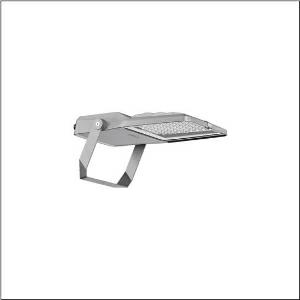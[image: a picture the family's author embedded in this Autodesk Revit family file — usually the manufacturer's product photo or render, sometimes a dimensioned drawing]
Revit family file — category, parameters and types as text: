
# Revit family: floodlight_fl_21_iq_mini___pl33t_5xa7771c4f1a_a815
name_source: partatom
category: Lighting Fixtures
units: mm (PartAtom-declared; Revit-internal decimal feet)

## family parameters
Cut with Voids When Loaded = No
Host = Face
Light Source = No
Part Type = Normal
Room Calculation Point = No
Round Connector Dimension = Use Diameter
Shared = No

## types (1)
- --- (1 x LED, 12570 lm, 87.2 W, 4000K)
    Apparent Load = 87 VA
    CIE Flux Codes = 26 75 99 100 100
    Color Rendering = 70
    Color Temperature = 4000K
    Default Elevation = 1800 mm
    Description = Floodlight FL 21 iQ mini, floodlight, primary light control with lens, of PMMA, primary optical cover: protective disc, of toughened safety glass, transparent, light distribution: PL33T, light emission: direct distribution, installation type: surface-mounted, lamps: LED, High Power LED, rated values: 12.570lm | 87,2W | 144,2lm/W (begin service life); end service life: 12.570lm | 92,1W; at 50% lumin. flux: 6.285lm | 40,2W | 156,3lm/W, colour temperature: 4000K, colour rendering: CRI > 70, light colour: 740, light setting 1 begin service life: 100% | 12.570lm | 87,2W | 144,2lm/W | 4.000K, light setting 1 end service life: 92,1W, further light settings possible, control: Auto-Match, Temp-Guard, Lumen-Switch, Night-Set, Smart-Wire, Light-Fading, Desk-Remote (wireless, voltage-free reading and setting of iQ features in the workshop via application-optimized NFC function/RFID function), optimised constant luminous flux control (CLO 2.0), pre-setting: linear dimming characteristic, with terminal, 6-pole, mains connection: 220..240V, AC, 50/60Hz, luminaire housing, of diecast aluminium, powder-coated, SITECO metallic grey (DB 702S), corrosivity category C5 mid according to DIN EN ISO 12944suitable for swimming poolschlorine-resistant, sealing non-destructively replaceable, mounting bracket, of steel, galvanised, powder-coated, SITECO metallic grey (DB 702S), protection rating (complete): IP66, insulation class (complete): insulation class II (safety insulation), certification: CE, ENEC, VDE, protection symbol: D, impact resistance: IK08, permissible operating ambient temperature: -40..+40°C, permissible operating ambient temperature for outdoor applications: -40..+50°C, standard: DIN EN 12944, LABS conformity tested according to VDMA 24364:2018-05, packaging unit: 1 piece

Light Distribution: PL33T
    Height = 70 mm
    Lamp = 1 x LED
    Lamp Light Flux = 12570 lm
    Lamp Power = 87.2 W
    Lamp count = 1
    Length = 485 mm
    Luminous efficacy = 144 lm/W
    Manufacturer = Siteco
    ModVariant = No
    Model = 5XA7771C4F1A
    Number of Poles = 1
    OnlyDefault = Yes
    Power Factor = 1
    Product Name = Floodlight FL 21 iQ mini | PL33T
    Product group = floodlight | pylon annexe
    ProductGroupID = 6201
    Protection Class = Protection class II
    Protection Degree = IP 66
    RLX_Detail_Level = 1
    RLX_Emergency_Light_Flux = 0 lm
    RLX_Emergency_Type = 0
    RLX_Emergency_Type_DB = No
    RlxData = <blob elided: 96445 chars, md5=9727f57c>
    Socket = socket
    Standby Power = 0 W
    System Light Flux = 12570 lm
    System Power = 87 W
    Type Comments = factory setting: luminous flux: 100 % | dim-lin: 254 | 456 mA
    Type Image = l_1006845.jpg
    URL = http://relux.com
    VarID = @adj_149203
    Voltage = 0 V
    Weight = 0.00 kg
    Width = 337 mm

## geometry (parser evidence)
native form markers: Blend x4, Sweep x14
no freeform markers — native parametric forms only
